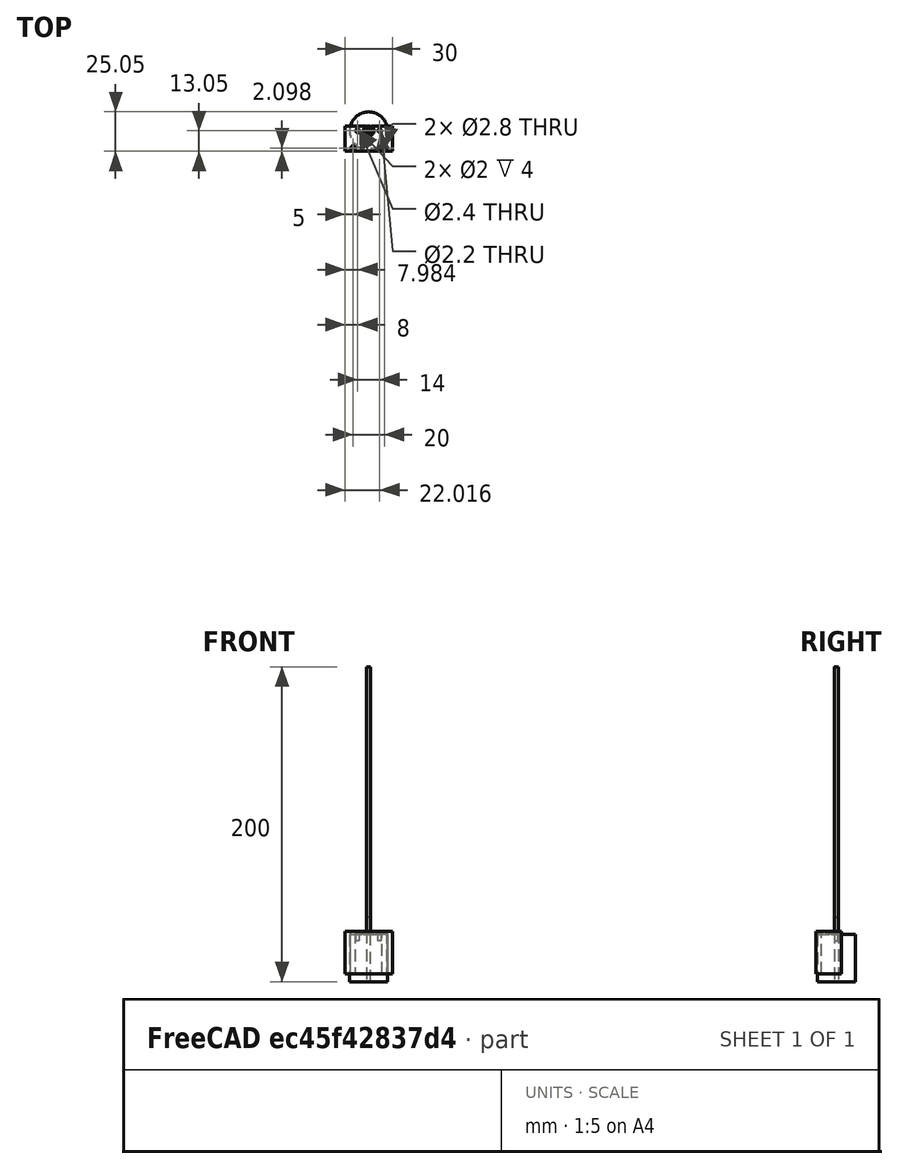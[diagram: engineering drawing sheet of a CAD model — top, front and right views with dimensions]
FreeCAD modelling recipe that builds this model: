
FCSTD DOCUMENT  (FreeCAD 0.19R24366 (Git))
Label: MotorAndHolder_v1
License: All rights reserved
LicenseURL: http://en.wikipedia.org/wiki/All_rights_reserved
objects: Sketcher::SketchObject×16, PartDesign::Pad×9, PartDesign::Pocket×9, PartDesign::Body×4, App::Part×4, Mesh::Feature×1
note: 56 computed .brp shape members not serialized (recipe doc carries the construction recipe); baked Part::Feature solids carry a one-line shape summary decoded from their .brp

FEATURE [Sketcher::SketchObject] Sketch
  FullyConstrained = false
  MapMode = 5
  Support = -> [XY_Plane001]
  sketch-geometry (1):
    g0: Circle CenterX=0 CenterY=0 CenterZ=0 NormalX=0 NormalY=0 NormalZ=1 AngleXU=0 Radius=12
  constraints (1):
    c: Radius(g0) = 12
FEATURE [PartDesign::Pad] Pad  label="MotorMain"
  Direction = (1,1,1)
  Length = 30
  Length2 = 100
  Profile = -> Sketch
  Type = 0
FEATURE [Sketcher::SketchObject] Sketch001
  FullyConstrained = true
  MapMode = 5
  Placement = pos=(0,0,30) rot=(0,0,1;0rad)
  Support = -> [Pad]
  sketch-geometry (1):
    g0: Circle CenterX=0 CenterY=0 CenterZ=0 NormalX=0 NormalY=0 NormalZ=1 AngleXU=0 Radius=3
  constraints (2):
    c: Coincident(g0,g-1)
    c: Radius(g0) = 3
FEATURE [PartDesign::Pad] Pad001  label="MotorHeader"
  BaseFeature = -> Pad
  Direction = (1,1,1)
  Length = 1
  Length2 = 100
  Profile = -> Sketch001
  Type = 0
FEATURE [Sketcher::SketchObject] Sketch002
  FullyConstrained = true
  MapMode = 5
  Placement = pos=(0,0,31) rot=(0,0,1;0rad)
  Support = -> [Pad001]
  sketch-geometry (1):
    g0: Circle CenterX=0 CenterY=0 CenterZ=0 NormalX=0 NormalY=0 NormalZ=1 AngleXU=0 Radius=1
  constraints (2):
    c: Coincident(g0,g-1)
    c: Radius(g0) = 1
FEATURE [PartDesign::Pad] Pad002  label="Shaft"
  BaseFeature = -> Pad001
  Direction = (1,1,1)
  Length = 10
  Length2 = 100
  Profile = -> Sketch002
  Type = 0
FEATURE [Sketcher::SketchObject] Sketch003
  FullyConstrained = true
  MapMode = 5
  Placement = pos=(0,0,30) rot=(0,0,1;0rad)
  Support = -> [Pad002]
  sketch-geometry (4):
    g0: Circle CenterX=-7 CenterY=0 CenterZ=0 NormalX=0 NormalY=0 NormalZ=1 AngleXU=0 Radius=1
    g1: Circle CenterX=7 CenterY=0 CenterZ=0 NormalX=0 NormalY=0 NormalZ=1 AngleXU=0 Radius=1
    g2: LineSegment StartX=-7 StartY=0 StartZ=0 EndX=0 EndY=0 EndZ=0
    g3: LineSegment StartX=0 StartY=0 StartZ=0 EndX=7 EndY=0 EndZ=0
  constraints (10):
    c: PointOnObject(g0,g-1)
    c: PointOnObject(g1,g-1)
    c: Diameter(g1) = 2
    c: Diameter(g0) = 2
    c: Coincident(g2,g0)
    c: Coincident(g2,g-1)
    c: Coincident(g3,g2)
    c: Coincident(g3,g1)
    c: Equal(g3,g2)
    c: DistanceX(g2,g2) = 7
FEATURE [PartDesign::Pocket] Pocket
  BaseFeature = -> Pad002
  Length = 4
  Length2 = 100
  Profile = -> Sketch003
  Type = 0
FEATURE [PartDesign::Body] Body  label="MotorBody"
  Group = -> [Sketch,Pad,Sketch001,Pad001,Sketch002,Pad002,Sketch003,Pocket]
  Origin = -> Origin001
  Tip = -> Pocket
FEATURE [App::Part] Part  label="MotorPart"
  Group = -> [Body]
  Origin = -> Origin
FEATURE [Sketcher::SketchObject] Sketch004
  FullyConstrained = false
  Placement = pos=(0,0,30) rot=(0,0,1;0rad)
  sketch-geometry (6):
    g0: LineSegment StartX=-15 StartY=2.95461 StartZ=0 EndX=15 EndY=2.95461 EndZ=0
    g1: LineSegment StartX=15 StartY=2.95461 StartZ=0 EndX=15 EndY=-13.0454 EndZ=0
    g2: LineSegment StartX=15 StartY=-13.0454 StartZ=0 EndX=-15 EndY=-13.0454 EndZ=0
    g3: LineSegment StartX=-15 StartY=-13.0454 StartZ=0 EndX=-15 EndY=2.95461 EndZ=0
    g4: LineSegment StartX=-15 StartY=0 StartZ=0 EndX=0 EndY=0 EndZ=0
    g5: LineSegment StartX=0 StartY=0 StartZ=0 EndX=15 EndY=0 EndZ=0
  constraints (17):
    c: Coincident(g0,g1)
    c: Coincident(g1,g2)
    c: Coincident(g2,g3)
    c: Coincident(g3,g0)
    c: Horizontal(g0)
    c: Horizontal(g2)
    c: Vertical(g1)
    c: Vertical(g3)
    c: DistanceY(g1,g1) = 16
    c: DistanceX(g0,g0) = 30
    c: PointOnObject(g4,g3)
    c: Coincident(g4,g-1)
    c: Horizontal(g4)
    c: PointOnObject(g5,g1)
    c: Horizontal(g5)
    c: Equal(g4,g5)
    c: Coincident(g5,g-1)
FEATURE [PartDesign::Pad] Pad003
  Direction = (1,1,1)
  Length = 2
  Length2 = 100
  Placement = pos=(0,0,30) rot=(0,0,1;0rad)
  Profile = -> Sketch004
  Type = 0
FEATURE [Sketcher::SketchObject] Sketch005
  FullyConstrained = true
  MapMode = 5
  Placement = pos=(0,0,30) rot=(0,0,1;0rad)
  Support = -> [Pad]
  sketch-geometry (1):
    g0: Circle CenterX=0 CenterY=0 CenterZ=0 NormalX=0 NormalY=0 NormalZ=1 AngleXU=0 Radius=3.4
  constraints (2):
    c: Coincident(g0,g-1)
    c: Radius(g0) = 3.4
FEATURE [PartDesign::Pocket] Pocket001
  BaseFeature = -> Pad003
  Length = 20
  Length2 = 100
  Placement = pos=(0,0,30) rot=(0,0,1;0rad)
  Profile = -> Sketch005
  Reversed = true
  Type = 0
FEATURE [PartDesign::Pad] Pad004
  BaseFeature = -> Pocket001
  Direction = (1,1,1)
  Length = 25
  Length2 = 100
  Placement = pos=(0,0,30) rot=(0,0,1;0rad)
  Profile = -> Sketch004
  Reversed = true
  Type = 0
FEATURE [Sketcher::SketchObject] Sketch006
  FullyConstrained = false
  MapMode = 5
  Support = -> [XY_Plane003]
  sketch-geometry (1):
    g0: Circle CenterX=0 CenterY=0 CenterZ=0 NormalX=0 NormalY=0 NormalZ=1 AngleXU=0 Radius=12.2
  constraints (1):
    c: Radius(g0) = 12.2
FEATURE [PartDesign::Pocket] Pocket002
  BaseFeature = -> Pad004
  Length = 30
  Length2 = 100
  Placement = pos=(0,0,30) rot=(0,0,1;0rad)
  Profile = -> Sketch006
  Reversed = true
  Type = 0
FEATURE [Sketcher::SketchObject] Sketch007
  FullyConstrained = false
  MapMode = 5
  Placement = pos=(0,0,32) rot=(0,0,1;0rad)
  Support = -> [Pocket002]
  sketch-geometry (4):
    g0: Circle CenterX=-7.01627 CenterY=0 CenterZ=0 NormalX=0 NormalY=0 NormalZ=1 AngleXU=0 Radius=1.2
    g1: Circle CenterX=7.01627 CenterY=0 CenterZ=0 NormalX=0 NormalY=0 NormalZ=1 AngleXU=0 Radius=1.1
    g2: LineSegment StartX=-7.01627 StartY=0 StartZ=0 EndX=0 EndY=0 EndZ=0
    g3: LineSegment StartX=0 StartY=0 StartZ=0 EndX=7.01627 EndY=0 EndZ=0
  constraints (9):
    c: PointOnObject(g0,g-1)
    c: PointOnObject(g1,g-1)
    c: Diameter(g1) = 2.2
    c: Diameter(g0) = 2.4
    c: Coincident(g2,g0)
    c: Coincident(g2,g-1)
    c: Coincident(g3,g2)
    c: Coincident(g3,g1)
    c: Equal(g3,g2)
FEATURE [PartDesign::Pocket] Pocket003
  BaseFeature = -> Pocket002
  Length = 5
  Length2 = 100
  Placement = pos=(0,0,30) rot=(0,0,1;0rad)
  Profile = -> Sketch007
  Type = 0
FEATURE [Sketcher::SketchObject] Sketch008
  FullyConstrained = false
  MapMode = 5
  Placement = pos=(0,0,32) rot=(0,0,1;0rad)
  Support = -> [Pocket003]
  sketch-geometry (4):
    g0: Circle CenterX=-10 CenterY=-10.9518 CenterZ=0 NormalX=0 NormalY=0 NormalZ=1 AngleXU=0 Radius=1.4
    g1: Circle CenterX=10 CenterY=-10.9518 CenterZ=0 NormalX=0 NormalY=0 NormalZ=1 AngleXU=0 Radius=1.4
    g2: LineSegment StartX=10 StartY=-10.9518 StartZ=0 EndX=0 EndY=-10.9518 EndZ=0
    g3: LineSegment StartX=-10 StartY=-10.9518 StartZ=0 EndX=0 EndY=-10.9518 EndZ=0
  constraints (10):
    c: Horizontal(g1,g0)
    c: Coincident(g2,g1)
    c: PointOnObject(g2,g-2)
    c: Horizontal(g2)
    c: Coincident(g3,g0)
    c: Coincident(g3,g2)
    c: Equal(g2,g3)
    c: DistanceX(g0,g1) = 20
    c: Equal(g0,g1)
    c: Diameter(g0) = 2.8
FEATURE [PartDesign::Pocket] Pocket004
  BaseFeature = -> Pocket003
  Length = 50
  Length2 = 100
  Placement = pos=(0,0,30) rot=(0,0,1;0rad)
  Profile = -> Sketch008
  Type = 0
FEATURE [PartDesign::Body] Body001  label="MotorHolderBody"
  Group = -> [Sketch004,Pad003,Sketch005,Pocket001,Pad004,Sketch006,Pocket002,Sketch007,Pocket003,Sketch008,Pocket004]
  Origin = -> Origin003
  Tip = -> Pocket004
FEATURE [App::Part] Part001  label="MotorHolder"
  Group = -> [Body001]
  Origin = -> Origin002
FEATURE [Mesh::Feature] Mesh  label="MotorHolder (Meshed)"
FEATURE [Sketcher::SketchObject] Sketch013
  FullyConstrained = true
  MapMode = 5
  Support = -> [XY_Plane012]
  sketch-geometry (1):
    g0: Circle CenterX=0 CenterY=0 CenterZ=0 NormalX=0 NormalY=0 NormalZ=1 AngleXU=0 Radius=1.25
  constraints (2):
    c: Coincident(g0,g-1)
    c: Diameter(g0) = 2.5
FEATURE [PartDesign::Pad] Pad006
  Direction = (1,1,1)
  Length = 200
  Length2 = 100
  Profile = -> Sketch013
  Type = 0
FEATURE [PartDesign::Body] Body006
  Group = -> [Sketch013,Pad006]
  Origin = -> Origin012
  Tip = -> Pad006
FEATURE [App::Part] Part006  label="ConnectorRod2.5x200mm001"
  Group = -> [Body006]
  Origin = -> Origin013
FEATURE [Sketcher::SketchObject] Sketch014
  FullyConstrained = false
  MapMode = 5
  Support = -> [XY_Plane015]
  sketch-geometry (1):
    g0: Circle CenterX=0 CenterY=0 CenterZ=0 NormalX=0 NormalY=0 NormalZ=1 AngleXU=0 Radius=12
  constraints (1):
    c: Radius(g0) = 12
FEATURE [PartDesign::Pad] Pad007  label="MotorMain001"
  Direction = (1,1,1)
  Length = 30
  Length2 = 100
  Profile = -> Sketch014
  Type = 0
FEATURE [Sketcher::SketchObject] Sketch017
  FullyConstrained = false
  Placement = pos=(0,0,30) rot=(0,0,1;0rad)
  sketch-geometry (6):
    g0: LineSegment StartX=-15 StartY=2.95461 StartZ=0 EndX=15 EndY=2.95461 EndZ=0
    g1: LineSegment StartX=15 StartY=2.95461 StartZ=0 EndX=15 EndY=-13.0454 EndZ=0
    g2: LineSegment StartX=15 StartY=-13.0454 StartZ=0 EndX=-15 EndY=-13.0454 EndZ=0
    g3: LineSegment StartX=-15 StartY=-13.0454 StartZ=0 EndX=-15 EndY=2.95461 EndZ=0
    g4: LineSegment StartX=-15 StartY=0 StartZ=0 EndX=0 EndY=0 EndZ=0
    g5: LineSegment StartX=0 StartY=0 StartZ=0 EndX=15 EndY=0 EndZ=0
  constraints (17):
    c: Coincident(g0,g1)
    c: Coincident(g1,g2)
    c: Coincident(g2,g3)
    c: Coincident(g3,g0)
    c: Horizontal(g0)
    c: Horizontal(g2)
    c: Vertical(g1)
    c: Vertical(g3)
    c: DistanceY(g1,g1) = 16
    c: DistanceX(g0,g0) = 30
    c: PointOnObject(g4,g3)
    c: Coincident(g4,g-1)
    c: Horizontal(g4)
    c: PointOnObject(g5,g1)
    c: Horizontal(g5)
    c: Equal(g4,g5)
    c: Coincident(g5,g-1)
FEATURE [PartDesign::Pad] Pad008
  Direction = (1,1,1)
  Length = 2
  Length2 = 100
  Placement = pos=(0,0,30) rot=(0,0,1;0rad)
  Profile = -> Sketch017
  Type = 0
FEATURE [Sketcher::SketchObject] Sketch018
  FullyConstrained = true
  MapMode = 5
  Placement = pos=(0,0,30) rot=(0,0,1;0rad)
  Support = -> [Pad007]
  sketch-geometry (1):
    g0: Circle CenterX=0 CenterY=0 CenterZ=0 NormalX=0 NormalY=0 NormalZ=1 AngleXU=0 Radius=3.4
  constraints (2):
    c: Coincident(g0,g-1)
    c: Radius(g0) = 3.4
FEATURE [PartDesign::Pocket] Pocket008
  BaseFeature = -> Pad008
  Length = 20
  Length2 = 100
  Placement = pos=(0,0,30) rot=(0,0,1;0rad)
  Profile = -> Sketch018
  Reversed = true
  Type = 0
FEATURE [PartDesign::Pad] Pad009
  BaseFeature = -> Pocket008
  Direction = (1,1,1)
  Length = 25
  Length2 = 100
  Placement = pos=(0,0,30) rot=(0,0,1;0rad)
  Profile = -> Sketch017
  Reversed = true
  Type = 0
FEATURE [Sketcher::SketchObject] Sketch019
  FullyConstrained = false
  MapMode = 5
  Support = -> [XY_Plane016]
  sketch-geometry (1):
    g0: Circle CenterX=0 CenterY=0 CenterZ=0 NormalX=0 NormalY=0 NormalZ=1 AngleXU=0 Radius=12.2
  constraints (1):
    c: Radius(g0) = 12.2
FEATURE [PartDesign::Pocket] Pocket005
  BaseFeature = -> Pad009
  Length = 30
  Length2 = 100
  Placement = pos=(0,0,30) rot=(0,0,1;0rad)
  Profile = -> Sketch019
  Reversed = true
  Type = 0
FEATURE [Sketcher::SketchObject] Sketch015
  FullyConstrained = false
  MapMode = 5
  Placement = pos=(0,0,32) rot=(0,0,1;0rad)
  Support = -> [Pocket005]
  sketch-geometry (4):
    g0: Circle CenterX=-7.01627 CenterY=0 CenterZ=0 NormalX=0 NormalY=0 NormalZ=1 AngleXU=0 Radius=1.2
    g1: Circle CenterX=7.01627 CenterY=0 CenterZ=0 NormalX=0 NormalY=0 NormalZ=1 AngleXU=0 Radius=1.1
    g2: LineSegment StartX=-7.01627 StartY=0 StartZ=0 EndX=0 EndY=0 EndZ=0
    g3: LineSegment StartX=0 StartY=0 StartZ=0 EndX=7.01627 EndY=0 EndZ=0
  constraints (9):
    c: PointOnObject(g0,g-1)
    c: PointOnObject(g1,g-1)
    c: Diameter(g1) = 2.2
    c: Diameter(g0) = 2.4
    c: Coincident(g2,g0)
    c: Coincident(g2,g-1)
    c: Coincident(g3,g2)
    c: Coincident(g3,g1)
    c: Equal(g3,g2)
FEATURE [PartDesign::Pocket] Pocket006
  BaseFeature = -> Pocket005
  Length = 5
  Length2 = 100
  Placement = pos=(0,0,30) rot=(0,0,1;0rad)
  Profile = -> Sketch015
  Type = 0
FEATURE [Sketcher::SketchObject] Sketch016
  FullyConstrained = false
  MapMode = 5
  Placement = pos=(0,0,32) rot=(0,0,1;0rad)
  Support = -> [Pocket006]
  sketch-geometry (4):
    g0: Circle CenterX=-10 CenterY=-10.9518 CenterZ=0 NormalX=0 NormalY=0 NormalZ=1 AngleXU=0 Radius=1.4
    g1: Circle CenterX=10 CenterY=-10.9518 CenterZ=0 NormalX=0 NormalY=0 NormalZ=1 AngleXU=0 Radius=1.4
    g2: LineSegment StartX=10 StartY=-10.9518 StartZ=0 EndX=0 EndY=-10.9518 EndZ=0
    g3: LineSegment StartX=-10 StartY=-10.9518 StartZ=0 EndX=0 EndY=-10.9518 EndZ=0
  constraints (10):
    c: Horizontal(g1,g0)
    c: Coincident(g2,g1)
    c: PointOnObject(g2,g-2)
    c: Horizontal(g2)
    c: Coincident(g3,g0)
    c: Coincident(g3,g2)
    c: Equal(g2,g3)
    c: DistanceX(g0,g1) = 20
    c: Equal(g0,g1)
    c: Diameter(g0) = 2.8
FEATURE [PartDesign::Pocket] Pocket007
  BaseFeature = -> Pocket006
  Length = 50
  Length2 = 100
  Placement = pos=(0,0,30) rot=(0,0,1;0rad)
  Profile = -> Sketch016
  Type = 0
FEATURE [PartDesign::Body] Body007  label="MotorHolderBody001"
  Group = -> [Sketch017,Pad008,Sketch018,Pocket008,Pad009,Sketch019,Pocket005,Sketch015,Pocket006,Sketch016,Pocket007]
  Origin = -> Origin014
  Tip = -> Pocket007
FEATURE [App::Part] Part007  label="MotorHolder001"
  Group = -> [Body007]
  Origin = -> Origin015
